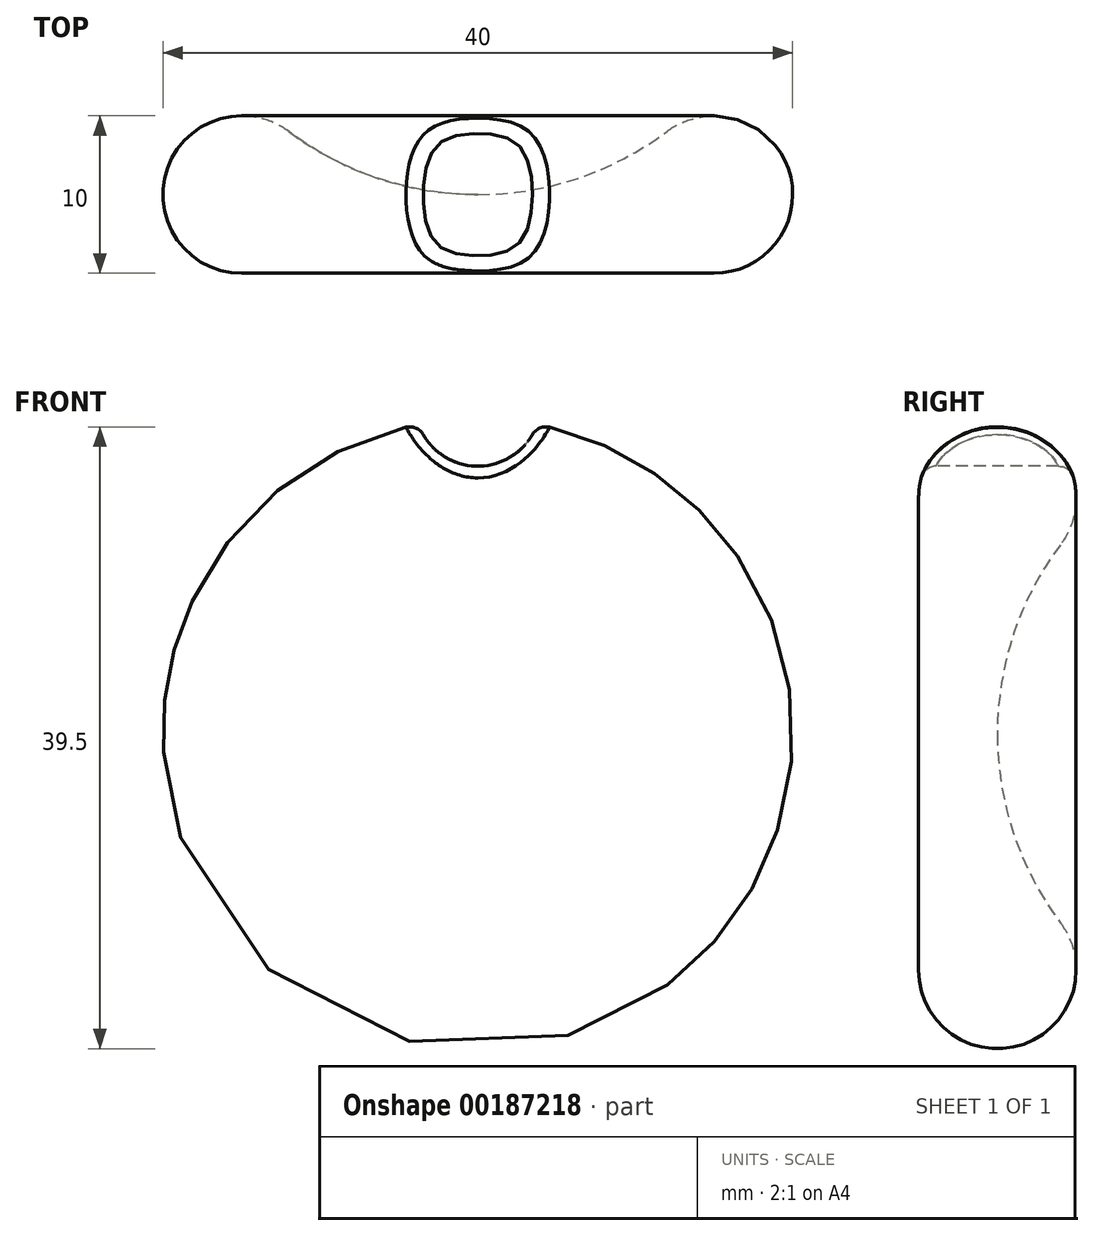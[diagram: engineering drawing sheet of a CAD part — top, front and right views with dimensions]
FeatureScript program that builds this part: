
annotation { "Feature Type Name" : "Feature", "Feature Type Description" : "" }
export const myFeature = defineFeature(function(context is Context, id is Id, definition is map)
    precondition{}
    {
        {
            var Q0;
            Q0=qCreatedBy(makeId("Top.planeOp"),FACE);
            var sketch = newSketch(context, id + "F0", { "sketchPlane" : qUnion([Q0])});
            skArc(sketch, "E0", {"start": v(-12, 9) * mm, "mid": v(-19.74, 6.58) * mm, "end": v(-15, 0) * mm});
            skArc(sketch, "E1", {"start": v(-12, 9) * mm, "mid": v(-6.32, 6.03) * mm, "end": v(0, 5) * mm});
            skLineSegment(sketch, "E2", {"start": v(0, 0) * mm, "end": v(0, 5) * mm});
            skLineSegment(sketch, "E3", {"start": v(0, 5) * mm, "end": v(0, 0) * mm});
            skLineSegment(sketch, "E4", {"start": v(0, 0) * mm, "end": v(-9.43, 0) * mm});
            skLineSegment(sketch, "E5", {"start": v(-9.43, 0) * mm, "end": v(0, 0) * mm});
            skLineSegment(sketch, "E6", {"start": v(-15, 0) * mm, "end": v(-9.43, 0) * mm});
            skSolve(sketch);
        }
        {
            var Q0;
            Q0=makeQuery(id+"F0.imprint","IMPRINT",FACE,{"disambiguationData":[TD([[makeQuery(id+"F0.imprint","IMPRINT",EDGE,{"derivedFrom":sQuery(id+"F0.wireOp",EDGE,"E0")}),1.0]])]});
            var Q1;
            Q1=sQuery(id+"F0.wireOp",EDGE,"E3");
            revolve(context, id + "F1", {"entities" : qUnion([Q0]), "axis" : qUnion([Q1]), "revolveType" : RevolveType.FULL});
        }
        {
            var Q0;
            Q0=qCreatedBy(makeId("Front.planeOp"),FACE);
            var sketch = newSketch(context, id + "F2", { "sketchPlane" : qUnion([Q0])});
            skLineSegment(sketch, "E7", {"start": v(-0.77, 0.62) * mm, "end": v(-3.45, -1.65) * mm});
            skLineSegment(sketch, "E8", {"start": v(-3.45, -1.65) * mm, "end": v(-0.22, 0.28) * mm});
            skLineSegment(sketch, "E9", {"start": v(-0.22, 0.28) * mm, "end": v(-0.77, 0.62) * mm});
            skLineSegment(sketch, "E10", {"start": v(-0.08, 0.55) * mm, "end": v(-0.01, 11.57) * mm});
            skLineSegment(sketch, "E11", {"start": v(-0.01, 11.57) * mm, "end": v(-0.63, 0.9) * mm});
            skLineSegment(sketch, "E12", {"start": v(-0.63, 0.9) * mm, "end": v(-0.08, 0.55) * mm});
            skLineSegment(sketch, "E13", {"start": v(0.4, 0.28) * mm, "end": v(9.22, -4.96) * mm});
            skLineSegment(sketch, "E14", {"start": v(9.22, -4.96) * mm, "end": v(1.1, 0.62) * mm});
            skLineSegment(sketch, "E15", {"start": v(1.1, 0.62) * mm, "end": v(0.4, 0.28) * mm});
            skArc(sketch, "E16", {"start": v(-8.62, -10.47) * mm, "mid": v(-4.52, -12.82) * mm, "end": v(0.13, -13.64) * mm});
            skArc(sketch, "E17", {"start": v(0.13, -13.64) * mm, "mid": v(5.4, -12.58) * mm, "end": v(9.86, -9.6) * mm});
            skArc(sketch, "E18", {"start": v(9.86, -9.6) * mm, "mid": v(12.85, -5.13) * mm, "end": v(13.9, 0.14) * mm});
            skArc(sketch, "E19", {"start": v(13.9, 0.14) * mm, "mid": v(13.66, 2.42) * mm, "end": v(13.04, 4.64) * mm});
            skArc(sketch, "E20", {"start": v(13.04, 4.64) * mm, "mid": v(12.6, 5.7) * mm, "end": v(12.06, 6.72) * mm});
            skArc(sketch, "E21", {"start": v(12.06, 6.72) * mm, "mid": v(11.43, 7.68) * mm, "end": v(10.6, 8.47) * mm});
            skArc(sketch, "E22", {"start": v(10.6, 8.47) * mm, "mid": v(12.75, 4.55) * mm, "end": v(13.5, 0.14) * mm});
            skArc(sketch, "E23", {"start": v(13.5, 0.14) * mm, "mid": v(12.47, -4.97) * mm, "end": v(9.57, -9.3) * mm});
            skArc(sketch, "E24", {"start": v(9.57, -9.3) * mm, "mid": v(5.24, -12.2) * mm, "end": v(0.13, -13.23) * mm});
            skArc(sketch, "E25", {"start": v(0.13, -13.23) * mm, "mid": v(-4.5, -12.4) * mm, "end": v(-8.55, -10.04) * mm});
            skArc(sketch, "E26", {"start": v(-8.55, -10.04) * mm, "mid": v(-11.54, -6.42) * mm, "end": v(-13.1, -2) * mm});
            skArc(sketch, "E27", {"start": v(-13.1, -2) * mm, "mid": v(-11.65, -6.65) * mm, "end": v(-8.62, -10.47) * mm});
            skArc(sketch, "E28", {"start": v(0.13, 13.85) * mm, "mid": v(5.4, 12.75) * mm, "end": v(9.91, 9.82) * mm});
            skArc(sketch, "E29", {"start": v(9.91, 9.82) * mm, "mid": v(13.1, 5.46) * mm, "end": v(14.32, 0.2) * mm});
            skArc(sketch, "E30", {"start": v(14.32, 0.2) * mm, "mid": v(13.25, 5.63) * mm, "end": v(10.17, 10.22) * mm});
            skArc(sketch, "E31", {"start": v(10.17, 10.22) * mm, "mid": v(5.56, 13.31) * mm, "end": v(0.13, 14.4) * mm});
            skArc(sketch, "E32", {"start": v(0.13, 14.4) * mm, "mid": v(-5.34, 13.34) * mm, "end": v(-9.98, 10.27) * mm});
            skArc(sketch, "E33", {"start": v(-9.98, 10.27) * mm, "mid": v(-13.1, 5.66) * mm, "end": v(-14.2, 0.2) * mm});
            skArc(sketch, "E34", {"start": v(-14.2, 0.2) * mm, "mid": v(-12.76, -6.03) * mm, "end": v(-8.76, -11.02) * mm});
            skArc(sketch, "E35", {"start": v(-8.76, -11.02) * mm, "mid": v(-9.92, -9.78) * mm, "end": v(-10.83, -8.33) * mm});
            skArc(sketch, "E36", {"start": v(-10.83, -8.33) * mm, "mid": v(-12.93, -4.3) * mm, "end": v(-13.65, 0.2) * mm});
            skArc(sketch, "E37", {"start": v(-13.65, 0.2) * mm, "mid": v(-12.6, 5.46) * mm, "end": v(-9.6, 9.9) * mm});
            skArc(sketch, "E38", {"start": v(-9.6, 9.9) * mm, "mid": v(-5.13, 12.82) * mm, "end": v(0.13, 13.85) * mm});
            skLineSegment(sketch, "E39", {"start": v(11.43, -6.4) * mm, "end": v(11.5, -6.34) * mm});
            skLineSegment(sketch, "E40", {"start": v(11.5, -6.34) * mm, "end": v(1.57, 0.9) * mm});
            skLineSegment(sketch, "E41", {"start": v(1.57, 0.9) * mm, "end": v(2.47, 1.45) * mm});
            skLineSegment(sketch, "E42", {"start": v(2.47, 1.45) * mm, "end": v(11.56, -6.2) * mm});
            skArc(sketch, "E43", {"start": v(11.56, -6.2) * mm, "mid": v(12.8, -3.14) * mm, "end": v(13.22, 0.14) * mm});
            skArc(sketch, "E44", {"start": v(13.22, 0.14) * mm, "mid": v(12.24, 5.12) * mm, "end": v(9.44, 9.36) * mm});
            skArc(sketch, "E45", {"start": v(9.44, 9.36) * mm, "mid": v(5.24, 12.2) * mm, "end": v(0.27, 13.23) * mm});
            skLineSegment(sketch, "E46", {"start": v(0.27, 13.23) * mm, "end": v(2.26, 1.8) * mm});
            skLineSegment(sketch, "E47", {"start": v(2.26, 1.8) * mm, "end": v(0.27, 0.55) * mm});
            skLineSegment(sketch, "E48", {"start": v(0.27, 0.55) * mm, "end": v(0.13, 13.23) * mm});
            skLineSegment(sketch, "E49", {"start": v(0.13, 13.23) * mm, "end": v(-0.01, 13.23) * mm});
            skLineSegment(sketch, "E50", {"start": v(-0.01, 13.23) * mm, "end": v(-1.18, 1.24) * mm});
            skLineSegment(sketch, "E51", {"start": v(-1.18, 1.24) * mm, "end": v(-1.94, 1.72) * mm});
            skLineSegment(sketch, "E52", {"start": v(-1.94, 1.72) * mm, "end": v(-0.22, 13.23) * mm});
            skArc(sketch, "E53", {"start": v(-0.22, 13.23) * mm, "mid": v(-5.14, 12.14) * mm, "end": v(-9.3, 9.29) * mm});
            skArc(sketch, "E54", {"start": v(-9.3, 9.29) * mm, "mid": v(-12.06, 5.08) * mm, "end": v(-13.03, 0.14) * mm});
            skArc(sketch, "E55", {"start": v(-13.03, 0.14) * mm, "mid": v(-12.6, -3.1) * mm, "end": v(-11.38, -6.13) * mm});
            skLineSegment(sketch, "E56", {"start": v(-11.38, -6.13) * mm, "end": v(-2.28, 1.45) * mm});
            skLineSegment(sketch, "E57", {"start": v(-2.28, 1.45) * mm, "end": v(-1.46, 0.9) * mm});
            skLineSegment(sketch, "E58", {"start": v(-1.46, 0.9) * mm, "end": v(-11.3, -6.27) * mm});
            skArc(sketch, "E59", {"start": v(-11.3, -6.27) * mm, "mid": v(-11.26, -6.33) * mm, "end": v(-11.24, -6.4) * mm});
            skLineSegment(sketch, "E60", {"start": v(-11.24, -6.4) * mm, "end": v(-0.08, 0) * mm});
            skLineSegment(sketch, "E61", {"start": v(-0.08, 0) * mm, "end": v(-0.08, -2.27) * mm});
            skLineSegment(sketch, "E62", {"start": v(-0.08, -2.27) * mm, "end": v(-11.1, -6.54) * mm});
            skArc(sketch, "E63", {"start": v(-11.1, -6.54) * mm, "mid": v(-6.34, -11.24) * mm, "end": v(0.13, -12.95) * mm});
            skArc(sketch, "E64", {"start": v(0.13, -12.95) * mm, "mid": v(6.6, -11.24) * mm, "end": v(11.36, -6.54) * mm});
            skLineSegment(sketch, "E65", {"start": v(11.36, -6.54) * mm, "end": v(0.27, -2.27) * mm});
            skLineSegment(sketch, "E66", {"start": v(0.27, -2.27) * mm, "end": v(0.27, 0) * mm});
            skLineSegment(sketch, "E67", {"start": v(0.27, 0) * mm, "end": v(11.5, -6.34) * mm});
            skLineSegment(sketch, "E68", {"start": v(11.5, -6.34) * mm, "end": v(11.43, -6.4) * mm});
            skArc(sketch, "E69", {"start": v(0.13, 14.67) * mm, "mid": v(-5.45, 13.57) * mm, "end": v(-10.2, 10.43) * mm});
            skArc(sketch, "E70", {"start": v(-10.2, 10.43) * mm, "mid": v(-13.36, 5.71) * mm, "end": v(-14.48, 0.14) * mm});
            skArc(sketch, "E71", {"start": v(-14.48, 0.14) * mm, "mid": v(-13.36, -5.43) * mm, "end": v(-10.18, -10.14) * mm});
            skArc(sketch, "E72", {"start": v(-10.18, -10.14) * mm, "mid": v(-5.45, -13.3) * mm, "end": v(0.13, -14.4) * mm});
            skArc(sketch, "E73", {"start": v(0.13, -14.4) * mm, "mid": v(5.69, -13.29) * mm, "end": v(10.4, -10.13) * mm});
            skArc(sketch, "E74", {"start": v(10.4, -10.13) * mm, "mid": v(13.54, -5.42) * mm, "end": v(14.66, 0.14) * mm});
            skArc(sketch, "E75", {"start": v(14.66, 0.14) * mm, "mid": v(13.56, 5.7) * mm, "end": v(10.4, 10.42) * mm});
            skArc(sketch, "E76", {"start": v(10.4, 10.42) * mm, "mid": v(5.69, 13.57) * mm, "end": v(0.13, 14.67) * mm});
            skLineSegment(sketch, "E77", {"start": v(-101.22, 47.57) * mm, "end": v(-101.22, -47.57) * mm});
            skLineSegment(sketch, "E78", {"start": v(-101.22, -47.57) * mm, "end": v(101.22, -47.57) * mm});
            skLineSegment(sketch, "E79", {"start": v(101.22, -47.57) * mm, "end": v(101.22, 47.57) * mm});
            skLineSegment(sketch, "E80", {"start": v(101.22, 47.57) * mm, "end": v(-101.22, 47.57) * mm});
            skSolve(sketch);
        }
        {
            var Q0;
            Q0 = qSketchRegion(id + "F2", true);
            extrude(context, id + "F3", {"entities" : qUnion([Q0]), "operationType" : NewBodyOperationType.REMOVE, "depth" : 25.4 * mm});
        }
        {
            var Q0;
            Q0=qCreatedBy(makeId("Top.planeOp"),FACE);
            var sketch = newSketch(context, id + "F4", { "sketchPlane" : qUnion([Q0])});
            skCircle(sketch, "E81", {"center": v(-15, 5) * mm, "radius": 4 * mm});
            skSolve(sketch);
        }
        {
            var Q0;
            Q0 = qSketchRegion(id + "F4", true);
            var Q1;
            Q1=sQuery(id+"F0.wireOp",EDGE,"E3");
            revolve(context, id + "F5", {"operationType" : NewBodyOperationType.ADD, "entities" : qUnion([Q0]), "axis" : qUnion([Q1]), "revolveType" : RevolveType.FULL});
        }
        {
            var Q0;
            Q0=qCreatedBy(makeId("Front.planeOp"),FACE);
            var sketch = newSketch(context, id + "F6", { "sketchPlane" : qUnion([Q0])});
            skCircle(sketch, "E82", {"center": v(0, 21) * mm, "radius": 4 * mm});
            skSolve(sketch);
        }
        {
            var Q0;
            Q0 = qSketchRegion(id + "F6", true);
            extrude(context, id + "F7", {"entities" : qUnion([Q0]), "operationType" : NewBodyOperationType.REMOVE, "oppositeDirection" : true, "depth" : 25.4 * mm});
        }
        {
            var Q0;
            Q0=makeQuery(id+"F7.boolean.opBoolean","INTERSECT",EDGE,{"derivedFrom":[makeQuery(id+"F1.opRevolve","SWEPT_FACE",FACE,{"disambiguationData":[OSD([sQuery(id+"F0.wireOp",EDGE,"E0")])]}),makeQuery(id+"F7.opExtrude","SWEPT_FACE",FACE,{"disambiguationData":[OSD([sQuery(id+"F6.wireOp",EDGE,"E82")])]})]});
            fillet(context, id + "F8", {"entities" : qUnion([Q0]), "radius" : 1 * mm, "tangentPropagation" : true, "allowEdgeOverflow" : false});
        }
    });
